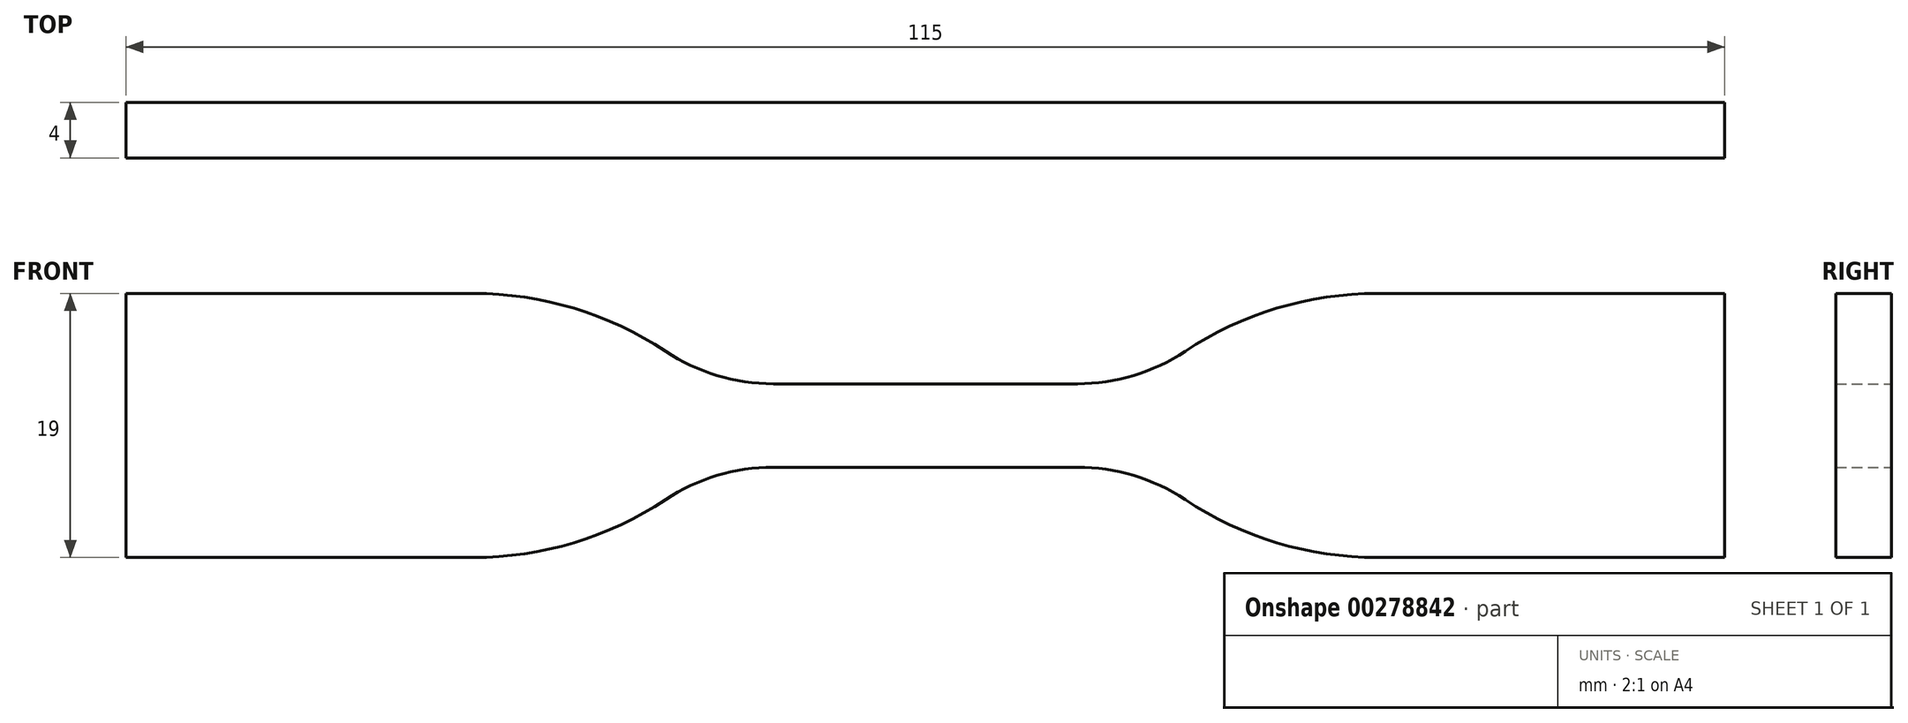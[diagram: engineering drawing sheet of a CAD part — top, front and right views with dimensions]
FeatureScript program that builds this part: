
annotation { "Feature Type Name" : "Feature", "Feature Type Description" : "" }
export const myFeature = defineFeature(function(context is Context, id is Id, definition is map)
    precondition{}
    {
        {
            var Q0;
            Q0=qCreatedBy(makeId("Front.planeOp"),FACE);
            var sketch = newSketch(context, id + "F0", { "sketchPlane" : qUnion([Q0])});
            skLineSegment(sketch, "E0", {"start": v(0, 3) * mm, "end": v(15.68, 3) * mm});
            skLineSegment(sketch, "E1", {"start": v(32.5, 9.5) * mm, "end": v(57.5, 9.5) * mm});
            skLineSegment(sketch, "E2", {"start": v(57.5, 9.5) * mm, "end": v(57.5, 0) * mm});
            skLineSegment(sketch, "E3.MirrorCS", {"start": v(57.5, -9.5) * mm, "end": v(57.5, 0) * mm});
            skLineSegment(sketch, "E4.MirrorCS", {"start": v(0, -3) * mm, "end": v(15.68, -3) * mm});
            skLineSegment(sketch, "E5.MirrorCS", {"start": v(32.5, -9.5) * mm, "end": v(57.5, -9.5) * mm});
            skLineSegment(sketch, "E6.MirrorCS", {"start": v(0, -3) * mm, "end": v(10.94, -3) * mm});
            skLineSegment(sketch, "E7.MirrorCS", {"start": v(0, 3) * mm, "end": v(10.94, 3) * mm});
            skLineSegment(sketch, "E8.MirrorCS", {"start": v(-57.5, -9.5) * mm, "end": v(-57.5, 0) * mm});
            skLineSegment(sketch, "E9.MirrorCS", {"start": v(-57.5, 9.5) * mm, "end": v(-57.5, 0) * mm});
            skLineSegment(sketch, "E10.MirrorCS", {"start": v(-32.5, 9.5) * mm, "end": v(-57.5, 9.5) * mm});
            skLineSegment(sketch, "E11.MirrorCS", {"start": v(-32.5, -9.5) * mm, "end": v(-57.5, -9.5) * mm});
            skLineSegment(sketch, "E12.MirrorCS", {"start": v(0, -3) * mm, "end": v(-10.94, -3) * mm});
            skLineSegment(sketch, "E13.MirrorCS", {"start": v(0, 3) * mm, "end": v(-10.94, 3) * mm});
            skLineSegment(sketch, "E14.MirrorCS", {"start": v(0, 3) * mm, "end": v(-15.68, 3) * mm});
            skLineSegment(sketch, "E15.MirrorCS", {"start": v(0, -3) * mm, "end": v(-15.68, -3) * mm});
            skArc(sketch, "E16", {"start": v(-18.68, 5.33) * mm, "mid": v(-25.28, 8.44) * mm, "end": v(-32.5, 9.5) * mm});
            skArc(sketch, "E17", {"start": v(32.5, 9.5) * mm, "mid": v(25.28, 8.44) * mm, "end": v(18.68, 5.33) * mm});
            skArc(sketch, "E18", {"start": v(18.68, -5.33) * mm, "mid": v(25.28, -8.44) * mm, "end": v(32.5, -9.5) * mm});
            skArc(sketch, "E19", {"start": v(-32.5, -9.5) * mm, "mid": v(-25.28, -8.44) * mm, "end": v(-18.68, -5.33) * mm});
            skPoint(sketch, "E20.visualSharp", {"position": v(-15.68, -3) * mm});
            skArc(sketch, "E20.filletArc", {"start": v(-10.94, -3) * mm, "mid": v(-14.98, -3.6) * mm, "end": v(-18.68, -5.33) * mm});
            skPoint(sketch, "E21.visualSharp", {"position": v(-15.68, 3) * mm});
            skArc(sketch, "E21.filletArc", {"start": v(-18.68, 5.33) * mm, "mid": v(-14.98, 3.6) * mm, "end": v(-10.94, 3) * mm});
            skPoint(sketch, "E22.visualSharp", {"position": v(15.68, 3) * mm});
            skArc(sketch, "E22.filletArc", {"start": v(10.94, 3) * mm, "mid": v(14.98, 3.6) * mm, "end": v(18.68, 5.33) * mm});
            skPoint(sketch, "E23.visualSharp", {"position": v(15.68, -3) * mm});
            skArc(sketch, "E23.filletArc", {"start": v(18.68, -5.33) * mm, "mid": v(14.98, -3.6) * mm, "end": v(10.94, -3) * mm});
            skSolve(sketch);
        }
        {
            var Q0;
            Q0=makeQuery(id+"F0.imprint","IMPRINT",FACE,{"disambiguationData":[TD([[makeQuery(id+"F0.imprint","IMPRINT",EDGE,{"derivedFrom":sQuery(id+"F0.wireOp",EDGE,"E3.MirrorCS")}),1.0]])]});
            extrude(context, id + "F1", {"entities" : qUnion([Q0]), "endBound" : BoundingType.SYMMETRIC, "depth" : 4 * mm});
        }
    });
